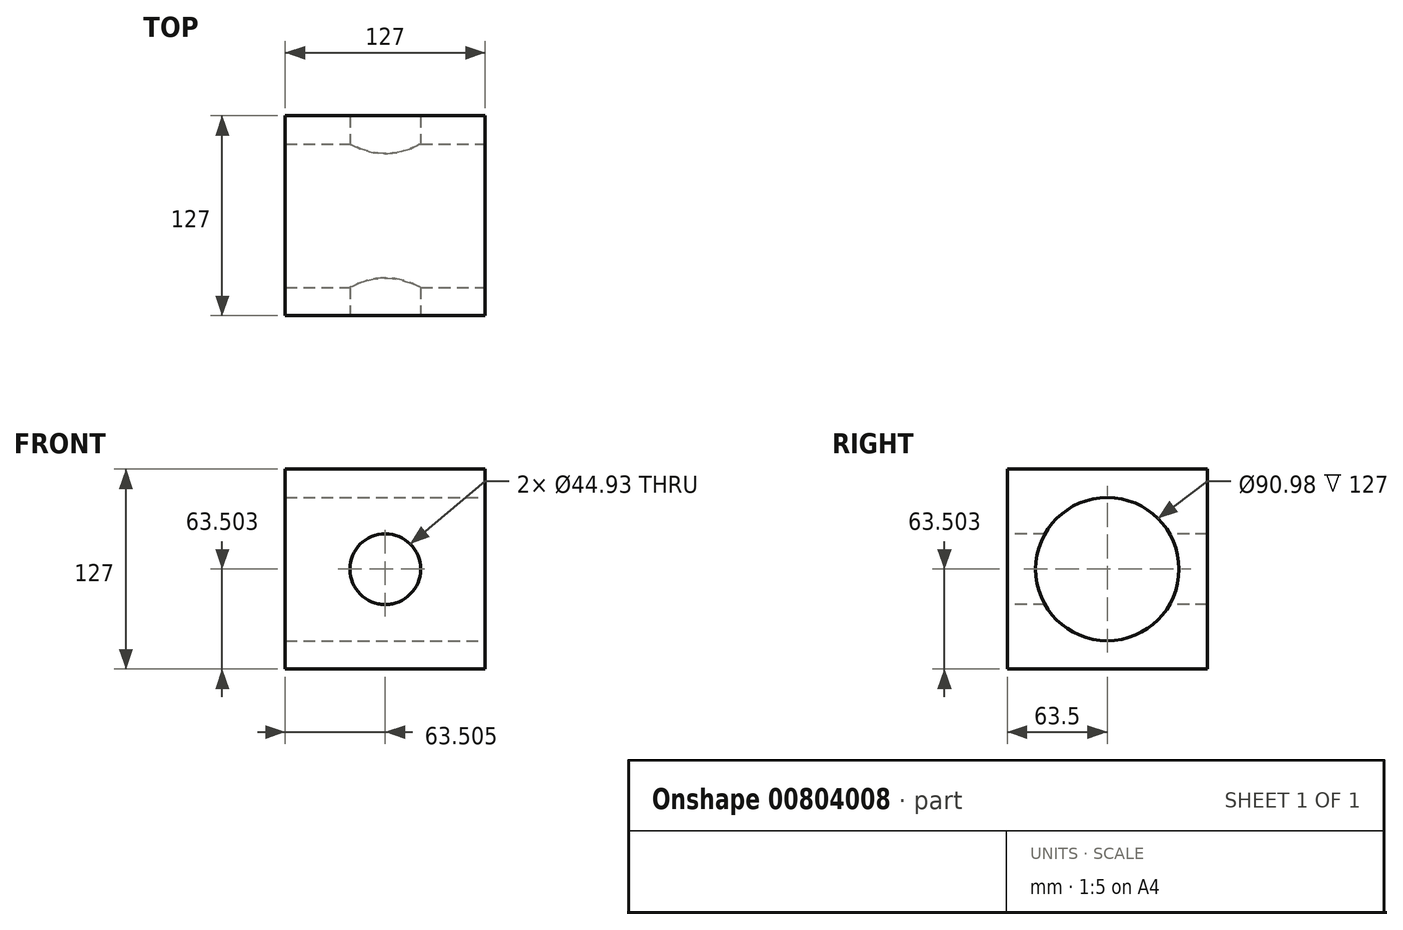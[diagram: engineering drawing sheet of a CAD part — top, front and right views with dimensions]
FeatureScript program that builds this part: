
annotation { "Feature Type Name" : "Feature", "Feature Type Description" : "" }
export const myFeature = defineFeature(function(context is Context, id is Id, definition is map)
    precondition{}
    {
        {
            var Q0;
            Q0=qCreatedBy(makeId("Front.planeOp"),FACE);
            var sketch = newSketch(context, id + "F0", { "sketchPlane" : qUnion([Q0])});
            skLineSegment(sketch, "E0.bottom", {"start": v(-53.06, 85.48) * mm, "end": v(73.94, 85.48) * mm});
            skLineSegment(sketch, "E0.top", {"start": v(-53.06, -41.52) * mm, "end": v(73.94, -41.52) * mm});
            skLineSegment(sketch, "E0.left", {"start": v(-53.06, 85.48) * mm, "end": v(-53.06, -41.52) * mm});
            skLineSegment(sketch, "E0.right", {"start": v(73.94, 85.48) * mm, "end": v(73.94, -41.52) * mm});
            skSolve(sketch);
        }
        {
            var Q0;
            Q0=makeQuery(id+"F0.imprint","IMPRINT",FACE,{"disambiguationData":[TD([[makeQuery(id+"F0.imprint","IMPRINT",EDGE,{"derivedFrom":sQuery(id+"F0.wireOp",EDGE,"E0.bottom")}),-1.0]])]});
            extrude(context, id + "F1", {"entities" : qUnion([Q0]), "depth" : 127 * mm, "offsetDistance" : 25.4 * mm});
        }
        {
            var Q0;
            Q0=makeQuery(id+"F1.opExtrude","CAP_FACE",FACE,{"disambiguationData":[OSD([sQuery(id+"F0.wireOp",EDGE,"E0.bottom"),sQuery(id+"F0.wireOp",EDGE,"E0.top"),sQuery(id+"F0.wireOp",EDGE,"E0.left"),sQuery(id+"F0.wireOp",EDGE,"E0.right")])],"isStart":false});
            var sketch = newSketch(context, id + "F2", { "sketchPlane" : qUnion([Q0])});
            skLineSegment(sketch, "E1", {"start": v(73.94, -41.52) * mm, "end": v(-53.06, -41.52) * mm});
            skCircle(sketch, "E2", {"center": v(10.44, 21.98) * mm, "radius": 22.47 * mm});
            skSolve(sketch);
        }
        {
            var Q0;
            Q0=makeQuery(id+"F2.imprint","IMPRINT",FACE,{"disambiguationData":[TD([[makeQuery(id+"F2.imprint","IMPRINT",EDGE,{"derivedFrom":sQuery(id+"F2.wireOp",EDGE,"E2")}),1.0]])]});
            extrude(context, id + "F3", {"entities" : qUnion([Q0]), "operationType" : NewBodyOperationType.REMOVE, "oppositeDirection" : true, "depth" : 145.03 * mm, "offsetDistance" : 25.4 * mm});
        }
        {
            var Q0;
            Q0=makeQuery(id+"F1.opExtrude","SWEPT_FACE",FACE,{"disambiguationData":[OSD([sQuery(id+"F0.wireOp",EDGE,"E0.right")])]});
            var sketch = newSketch(context, id + "F4", { "sketchPlane" : qUnion([Q0])});
            skLineSegment(sketch, "E3", {"start": v(-127, -41.52) * mm, "end": v(0, -41.52) * mm});
            skCircle(sketch, "E4", {"center": v(-63.5, 21.98) * mm, "radius": 45.5 * mm});
            skSolve(sketch);
        }
        {
            var Q0;
            Q0=makeQuery(id+"F4.imprint","IMPRINT",FACE,{"disambiguationData":[TD([[makeQuery(id+"F4.imprint","IMPRINT",EDGE,{"derivedFrom":sQuery(id+"F4.wireOp",EDGE,"E4")}),1.0]])]});
            var Q1;
            Q1=sQuery(id+"F4.wireOp",EDGE,"E4");
            extrude(context, id + "F5", {"entities" : qUnion([Q0]), "operationType" : NewBodyOperationType.REMOVE, "surfaceEntities" : qUnion([Q1]), "oppositeDirection" : true, "depth" : 141.48 * mm, "offsetDistance" : 25.4 * mm});
        }
    });
